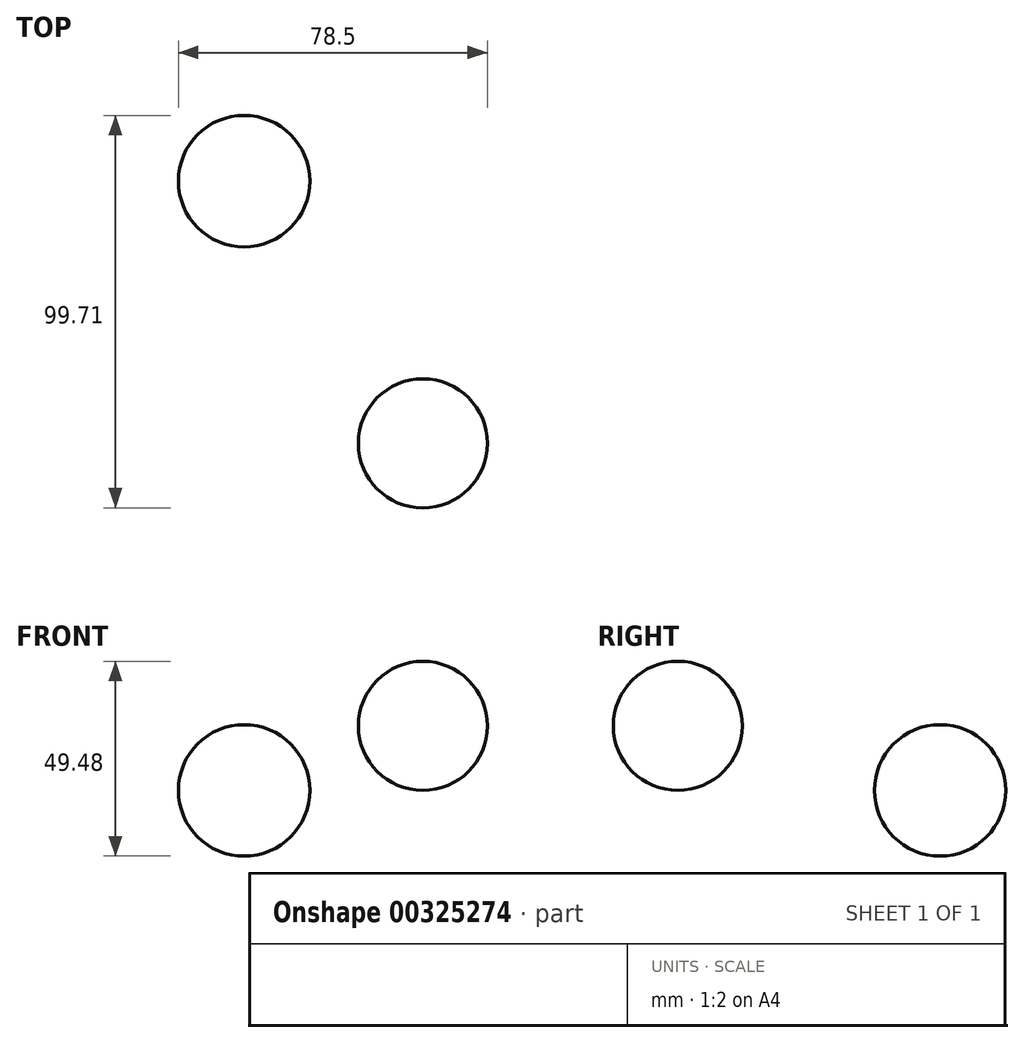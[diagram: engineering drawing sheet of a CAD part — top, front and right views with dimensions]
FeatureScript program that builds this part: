
annotation { "Feature Type Name" : "Feature", "Feature Type Description" : "" }
export const myFeature = defineFeature(function(context is Context, id is Id, definition is map)
    precondition{}
    {
        {
            var Q0;
            Q0=qCreatedBy(makeId("Top.planeOp"),FACE);
            var sketch = newSketch(context, id + "F0", { "sketchPlane" : qUnion([Q0])});
            skLineSegment(sketch, "E0", {"start": v(-45.42, 33.39) * mm, "end": v(-45.42, 0) * mm});
            skArc(sketch, "E1", {"start": v(-45.42, 33.39) * mm, "mid": v(-28.73, 16.7) * mm, "end": v(-45.42, 0) * mm});
            skSolve(sketch);
        }
        {
            var Q0;
            Q0=makeQuery(id+"F0.imprint","IMPRINT",FACE,{"disambiguationData":[TD([[makeQuery(id+"F0.imprint","IMPRINT",EDGE,{"derivedFrom":sQuery(id+"F0.wireOp",EDGE,"E0")}),1.0]])]});
            var Q1;
            Q1=sQuery(id+"F0.wireOp",EDGE,"E0");
            revolve(context, id + "F1", {"entities" : qUnion([Q0]), "axis" : qUnion([Q1]), "revolveType" : RevolveType.FULL});
        }
        {
            var Q0;
            Q0=qCreatedBy(makeId("Right.planeOp"),FACE);
            var sketch = newSketch(context, id + "F2", { "sketchPlane" : qUnion([Q0])});
            skLineSegment(sketch, "E2", {"start": v(-49.93, 32.79) * mm, "end": v(-49.93, 0) * mm});
            skArc(sketch, "E3", {"start": v(-49.93, 32.79) * mm, "mid": v(-33.54, 16.4) * mm, "end": v(-49.93, 0) * mm});
            skSolve(sketch);
        }
        {
            var Q0;
            Q0=makeQuery(id+"F2.imprint","IMPRINT",FACE,{"disambiguationData":[TD([[makeQuery(id+"F2.imprint","IMPRINT",EDGE,{"derivedFrom":sQuery(id+"F2.wireOp",EDGE,"E2")}),1.0]])]});
            var Q1;
            Q1=sQuery(id+"F2.wireOp",EDGE,"E2");
            revolve(context, id + "F3", {"entities" : qUnion([Q0]), "axis" : qUnion([Q1]), "revolveType" : RevolveType.FULL});
        }
    });
